# Revit family: Gitterinnen-Systeme_Gitterrinne_GR-Magic_55_300
name_source: partatom
category: Generic Models
revit_build: Autodesk Revit 2015 (Build: 20140606_1530(x64)
units: mm (PartAtom-declared; Revit-internal decimal feet)

## types (10) — shared parameters
Manufacturer = OBO Bettermann
URL = http://www.obo-bettermann.com

## per-type parameters (varying)
| type | GTIN | Manufacturer Art. No. | Material |
| GRM 55 300 FT | 4012196815050 | 6001424 | Steel, Galvanized |
| GRM 55 300 G | 4012196858675 | 6001448 | Steel, Galvanized |
| GRM 55 300 VA4301 | 4012196101771 | 6001078 | Stainless Steel |
| GRM 55 300 VA4401 | 4012195166078 | 6001093 | Stainless Steel |
| GRM 55 300 LGR | 4012195958789 | 7250046 | Steel, Galvanized |
| GRM 55 300 GC | 4012195068679 | 6001028 | Steel, Galvanized |
| GRM 55 300 F | 4012196323531 | 6001050 | Steel, Galvanized |
| GRM 55 300 FT SO | 4012195979975 | 7196702 | Steel, Galvanized |
| GRM 55 300 FTKSGR | 4012195979661 | 6479221 | Steel, Galvanized |
| GRM 55 300 FTK | 4012196859030 | 7250016 | Steel, Galvanized |

note: column(s) folded — value = type name in every type: Article Type

## geometry (parser evidence)
native form markers: Sweep x3
no freeform markers — native parametric forms only
